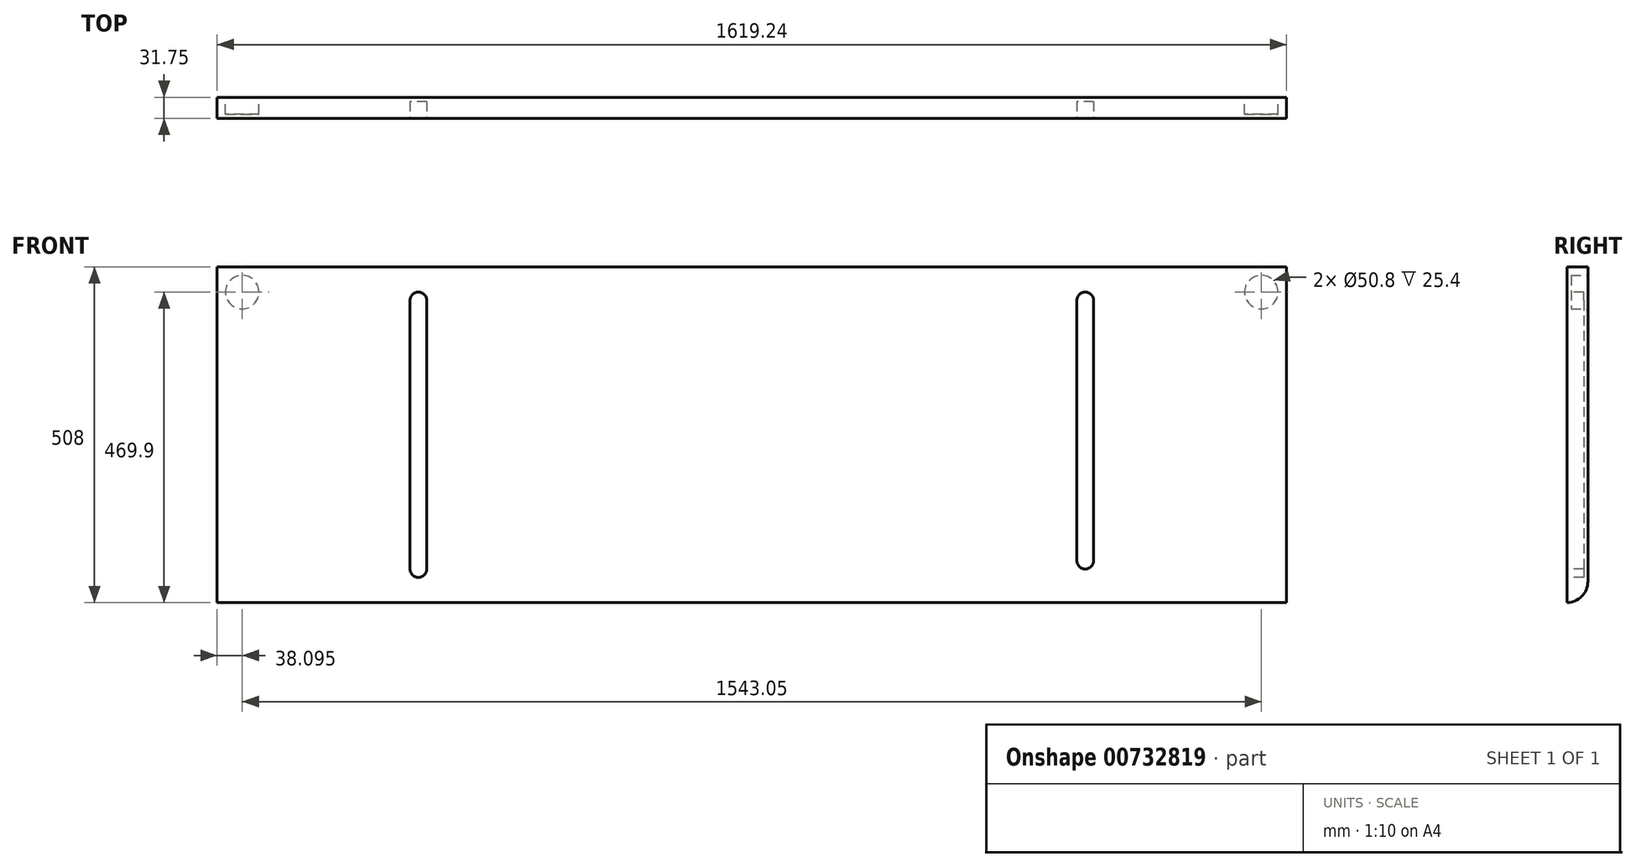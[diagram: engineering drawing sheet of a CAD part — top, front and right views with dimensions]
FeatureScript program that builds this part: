
annotation { "Feature Type Name" : "Feature", "Feature Type Description" : "" }
export const myFeature = defineFeature(function(context is Context, id is Id, definition is map)
    precondition{}
    {
        {
            var Q0;
            Q0=qCreatedBy(makeId("Front.planeOp"),FACE);
            var sketch = newSketch(context, id + "F0", { "sketchPlane" : qUnion([Q0])});
            skLineSegment(sketch, "E0.bottom", {"start": v(-809.63, 254) * mm, "end": v(809.62, 254) * mm});
            skLineSegment(sketch, "E0.top", {"start": v(-809.63, -254) * mm, "end": v(809.62, -254) * mm});
            skLineSegment(sketch, "E0.left", {"start": v(-809.63, 254) * mm, "end": v(-809.63, -254) * mm});
            skLineSegment(sketch, "E0.right", {"start": v(809.62, 254) * mm, "end": v(809.62, -254) * mm});
            skPoint(sketch, "E0.middle", {"position": v(0, 0) * mm});
            skSolve(sketch);
        }
        {
            var Q0;
            Q0 = qSketchRegion(id + "F0", true);
            extrude(context, id + "F1", {"entities" : qUnion([Q0]), "depth" : 31.75 * mm, "offsetDistance" : 25.4 * mm});
        }
        {
            var Q0;
            Q0=makeQuery(id+"F1.opExtrude","SWEPT_FACE",FACE,{"disambiguationData":[OSD([sQuery(id+"F0.wireOp",EDGE,"E0.left")])]});
            var sketch = newSketch(context, id + "F2", { "sketchPlane" : qUnion([Q0])});
            skLineSegment(sketch, "E1", {"start": v(0, -254) * mm, "end": v(0, -222.25) * mm});
            skLineSegment(sketch, "E2", {"start": v(0, -222.25) * mm, "end": v(0, -254) * mm});
            skLineSegment(sketch, "E3", {"start": v(0, -254) * mm, "end": v(31.75, -254) * mm});
            skArc(sketch, "E4", {"start": v(0, -222.25) * mm, "mid": v(9.3, -244.7) * mm, "end": v(31.75, -254) * mm});
            skSolve(sketch);
        }
        {
            var Q0;
            Q0 = qSketchRegion(id + "F2", true);
            extrude(context, id + "F3", {"entities" : qUnion([Q0]), "operationType" : NewBodyOperationType.REMOVE, "endBound" : BoundingType.THROUGH_ALL, "oppositeDirection" : true, "depth" : 25.4 * mm, "offsetDistance" : 25.4 * mm});
        }
        {
            var Q0;
            Q0=makeQuery(id+"F1.opExtrude","CAP_FACE",FACE,{"disambiguationData":[OSD([sQuery(id+"F0.wireOp",EDGE,"E0.bottom"),sQuery(id+"F0.wireOp",EDGE,"E0.top"),sQuery(id+"F0.wireOp",EDGE,"E0.left"),sQuery(id+"F0.wireOp",EDGE,"E0.right")])],"isStart":false});
            var sketch = newSketch(context, id + "F4", { "sketchPlane" : qUnion([Q0])});
            skArc(sketch, "E5", {"start": v(-492.13, 203.2) * mm, "mid": v(-504.83, 215.9) * mm, "end": v(-517.53, 203.2) * mm});
            skArc(sketch, "E6", {"start": v(517.53, 203.2) * mm, "mid": v(504.83, 215.9) * mm, "end": v(492.13, 203.2) * mm});
            skArc(sketch, "E7", {"start": v(-517.53, -203.2) * mm, "mid": v(-504.83, -215.9) * mm, "end": v(-492.13, -203.2) * mm});
            skArc(sketch, "E8", {"start": v(492.13, -190.5) * mm, "mid": v(504.83, -203.2) * mm, "end": v(517.53, -190.5) * mm});
            skLineSegment(sketch, "E9", {"start": v(-517.53, 203.2) * mm, "end": v(-517.53, -203.2) * mm});
            skLineSegment(sketch, "E10", {"start": v(-492.13, -203.2) * mm, "end": v(-492.13, 203.2) * mm});
            skLineSegment(sketch, "E11", {"start": v(492.13, 203.2) * mm, "end": v(492.13, -190.5) * mm});
            skLineSegment(sketch, "E12", {"start": v(517.53, -190.5) * mm, "end": v(517.53, 203.2) * mm});
            skSolve(sketch);
        }
        {
            var Q0;
            Q0 = qSketchRegion(id + "F4", true);
            extrude(context, id + "F5", {"entities" : qUnion([Q0]), "operationType" : NewBodyOperationType.REMOVE, "oppositeDirection" : true, "depth" : 25.4 * mm, "offsetDistance" : 25.4 * mm});
        }
        {
            var Q0;
            Q0=makeQuery(id+"F1.opExtrude","CAP_FACE",FACE,{"disambiguationData":[OSD([sQuery(id+"F0.wireOp",EDGE,"E0.bottom"),sQuery(id+"F0.wireOp",EDGE,"E0.top"),sQuery(id+"F0.wireOp",EDGE,"E0.left"),sQuery(id+"F0.wireOp",EDGE,"E0.right")])],"isStart":true});
            var sketch = newSketch(context, id + "F6", { "sketchPlane" : qUnion([Q0])});
            skCircle(sketch, "E13", {"center": v(-771.52, 215.9) * mm, "radius": 25.4 * mm});
            skCircle(sketch, "E14", {"center": v(771.53, 215.9) * mm, "radius": 25.4 * mm});
            skSolve(sketch);
        }
        {
            var Q0;
            Q0 = qSketchRegion(id + "F6", true);
            extrude(context, id + "F7", {"entities" : qUnion([Q0]), "operationType" : NewBodyOperationType.REMOVE, "oppositeDirection" : true, "depth" : 25.4 * mm, "offsetDistance" : 25.4 * mm});
        }
    });
